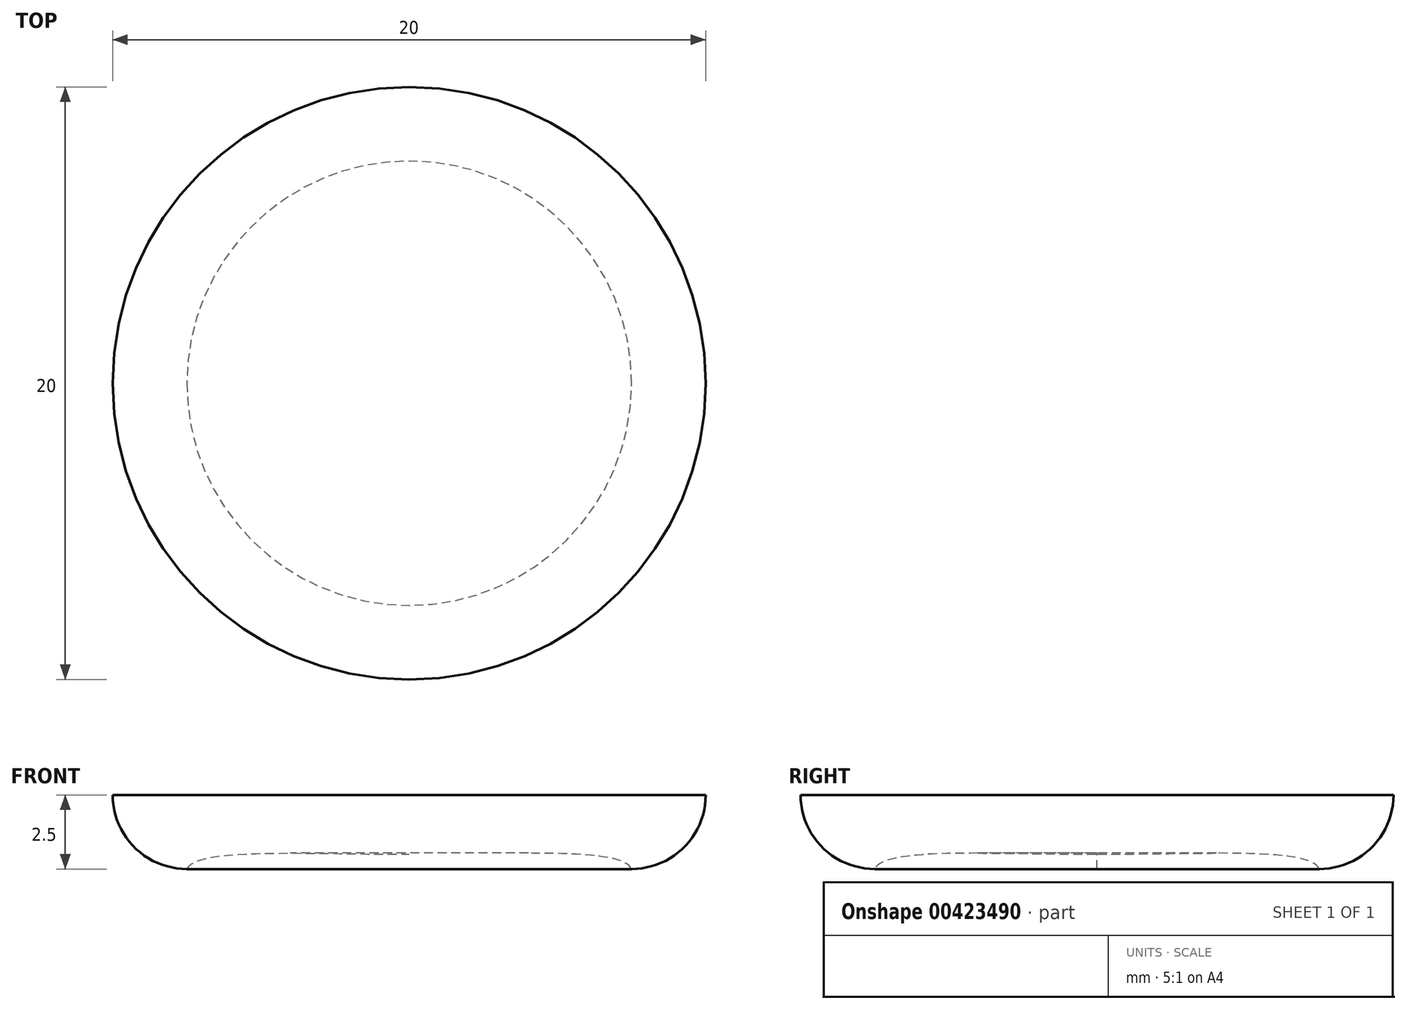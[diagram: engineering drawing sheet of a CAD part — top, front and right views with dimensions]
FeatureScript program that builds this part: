
annotation { "Feature Type Name" : "Feature", "Feature Type Description" : "" }
export const myFeature = defineFeature(function(context is Context, id is Id, definition is map)
    precondition{}
    {
        {
            var Q0;
            Q0=qCreatedBy(makeId("Front.planeOp"),FACE);
            var sketch = newSketch(context, id + "F0", { "sketchPlane" : qUnion([Q0])});
            skLineSegment(sketch, "E0.left", {"start": v(-4, 2) * mm, "end": v(-4, -2) * mm});
            skPoint(sketch, "E1.endSnap0", {"position": v(0, 2) * mm});
            skLineSegment(sketch, "E2", {"start": v(0, -2) * mm, "end": v(-10, -2) * mm});
            skLineSegment(sketch, "E3", {"start": v(0, -2) * mm, "end": v(0, -4) * mm});
            skLineSegment(sketch, "E4", {"start": v(-10, -2) * mm, "end": v(-10, -2) * mm});
            skPoint(sketch, "E5.visualSharp", {"position": v(-10, -4.5) * mm});
            skArc(sketch, "E5.filletArc", {"start": v(-10, -2) * mm, "mid": v(-9.27, -3.77) * mm, "end": v(-7.5, -4.5) * mm});
            skFitSpline(sketch, "E6", {"points": [v(-7.5, -4.5) * mm, v(0, -4) * mm], "startDerivative": vector(1, 2.2) * mm, "endDerivative": vector(11.01, 0) * mm});
            skLineSegment(sketch, "E7", {"start": v(-4, -2) * mm, "end": v(-4, 2) * mm});
            skLineSegment(sketch, "E8", {"start": v(-4, 2) * mm, "end": v(-2.5, 2) * mm});
            skLineSegment(sketch, "E9", {"start": v(-2.5, -0.5) * mm, "end": v(-2.5, 2) * mm});
            skLineSegment(sketch, "E10", {"start": v(-2.5, -0.5) * mm, "end": v(0, -0.5) * mm});
            skLineSegment(sketch, "E11", {"start": v(0, -0.5) * mm, "end": v(0, -2) * mm});
            skSolve(sketch);
        }
        {
            var Q0;
            {var subQ1=sQuery(id+"F0.wireOp",EDGE,"E3");Q0=makeQuery(id+"F0.imprint","IMPRINT",FACE,{"disambiguationData":[TD([[makeQuery(id+"F0.imprint","IMPRINT",EDGE,{"derivedFrom":subQ1}),-1.0]])]});}
            var Q1;
            {var subQ0=sQuery(id+"F0.wireOp",EDGE,"E7");Q1=makeQuery(id+"F0.imprint","IMPRINT",FACE,{"disambiguationData":[TD([[makeQuery(id+"F0.imprint","IMPRINT",EDGE,{"derivedFrom":subQ0}),-1.0]])]});}
            var Q2;
            Q2=sQuery(id+"F0.wireOp",EDGE,"E3");
            revolve(context, id + "F1", {"entities" : qUnion([Q0, Q1]), "axis" : qUnion([Q2]), "revolveType" : RevolveType.FULL});
        }
    });
